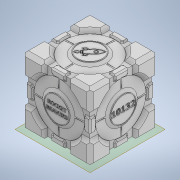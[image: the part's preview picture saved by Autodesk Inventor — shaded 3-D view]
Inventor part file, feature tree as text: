
AUTODESK INVENTOR PART (.ipt)
format: ipt  version: 2020 (Build 240168000, 168)  size: 2,784,256 bytes
history: native  units: in
note: dims shown in document units (in); Inventor stores cm internally (conversion verified against a paired STEP export)
features: other x9, sketch x7, extrude x4, chamfer x4, emboss x4, fillet x2, boolean_combine x1, plane x1
ambient origin geometry x8: Origin, YZ Plane, XZ Plane, XY Plane, X Axis, Y Axis, Z Axis, Center Point
bodies: Solid1 (feature_tree), Solid2 (feature_tree), Solid3 (feature_tree), Solid4 (feature_tree), Solid5 (feature_tree), Solid6 (feature_tree), Solid7 (feature_tree), Solid8 (feature_tree)
feature tree (32):
  other  "Portal Companion Cube.iam"
  other  "Portal Companion Cube.ipt:1"
  other  "Portal Companion Cube.ipt:2"
  other  "Portal Companion Cube.ipt:3"
  other  "Portal Companion Cube.ipt:4"
  other  "Portal Companion Cube_MIR.ipt:1"
  other  "Portal Companion Cube_MIR.ipt:2"
  other  "Portal Companion Cube_MIR.ipt:3"
  other  "Portal Companion Cube_MIR.ipt:4"
  boolean_combine  "Combine1"
  plane  "Work Plane1"
  extrude  "Extrusion1"  Depth=0.3937in
  extrude  "Extrusion2"  Depth=0.175in
  extrude  "Extrusion3"  Depth=0.3in TaperAngle=0.0deg
  chamfer  "Chamfer1"  Distance=0.05in
  chamfer  "Chamfer2"  Distance=0.0375in
  chamfer  "Chamfer3"  Distance=0.25in
  chamfer  "Chamfer4"  Distance=0.0375in Angle=45.0deg
  fillet  "Fillet1"  Radius=0.0375in
  fillet  "Fillet2"  Radius=0.0375in
  sketch  "Sketch4"  dims[d7=0.74in d8=0.05in d9=0.0in]
  sketch  "Sketch5"  dims[d10=0.0375in]
  sketch  "Sketch6"  dims[d11=0.0375in]
  emboss  "Emboss1"
  emboss  "Emboss2"
  emboss  "Emboss3"
  emboss  "Emboss4"
  extrude  "Extrusion4"  Depth=0.05in TaperAngle=45.0deg
  sketch  "Sketch1"  dims[d0=0.3937in d1=0.175in]
  sketch  "Sketch2"  dims[d2=0.175in d3=0.175in]
  sketch  "Sketch3"  dims[d4=0.175in d5=0.3in d6=0.0in]
  sketch  "Sketch7"  dims[d12=0.0375in d13=0.0375in d14=0.25in d15=0.0in d16=0.0375in d17=0.25in d18=45.0deg d19=0.0375in d20=0.25in d21=45.0deg d22=0.0375in d23=0.25in d24=45.0deg d25=0.0375in d26=0.25in d27=45.0deg d28=0.02in d29=0.02in d30=0.05in d31=0.0in d32=0.05in d33=0.0in d34=0.05in d35=0.0in d36=0.05in d37=0.0in d69=0.05in d70=0.0in d71=0.5in d72=0.0344in]
